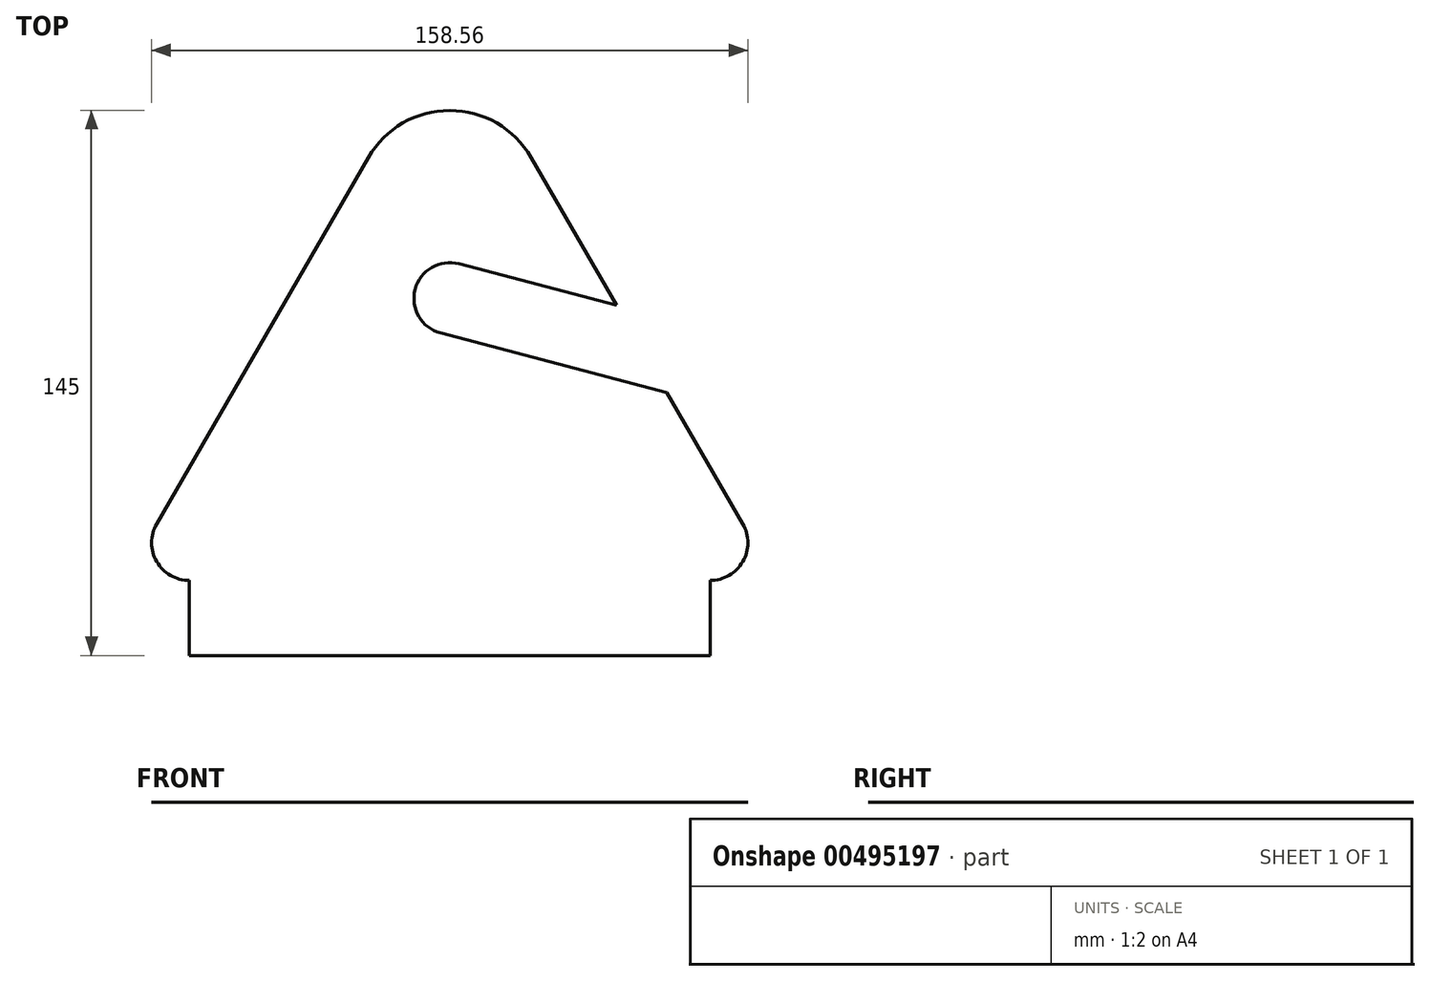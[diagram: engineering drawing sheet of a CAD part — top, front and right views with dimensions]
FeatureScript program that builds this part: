
annotation { "Feature Type Name" : "Feature", "Feature Type Description" : "" }
export const myFeature = defineFeature(function(context is Context, id is Id, definition is map)
    precondition{}
    {
        {
            var Q0;
            Q0=qCreatedBy(makeId("Top.planeOp"),FACE);
            var sketch = newSketch(context, id + "F0", { "sketchPlane" : qUnion([Q0])});
            skCircle(sketch, "E0", {"center": v(0, 0) * mm, "radius": 50 * mm, "construction": true});
            skLineSegment(sketch, "E1", {"start": v(0, 0) * mm, "end": v(0, 100) * mm, "construction": true});
            skLineSegment(sketch, "E2", {"start": v(0, 0) * mm, "end": v(-86.6, -50) * mm, "construction": true});
            skLineSegment(sketch, "E3", {"start": v(-86.6, -50) * mm, "end": v(0, 100) * mm, "construction": true});
            skCircle(sketch, "E4", {"center": v(0, 50) * mm, "radius": 25 * mm, "construction": true});
            skPoint(sketch, "E5", {"position": v(-69.28, -40) * mm});
            skCircle(sketch, "E6", {"center": v(-69.28, -40) * mm, "radius": 10 * mm, "construction": true});
            skCircle(sketch, "E7.MirrorC", {"center": v(69.28, -40) * mm, "radius": 10 * mm, "construction": true});
            skLineSegment(sketch, "E8.MirrorCS", {"start": v(0, 0) * mm, "end": v(86.6, -50) * mm, "construction": true});
            skLineSegment(sketch, "E9", {"start": v(0, 100) * mm, "end": v(86.6, -50) * mm, "construction": true});
            skLineSegment(sketch, "E10", {"start": v(86.6, -50) * mm, "end": v(-86.6, -50) * mm, "construction": true});
            skArc(sketch, "E11", {"start": v(21.65, 62.5) * mm, "mid": v(0, 75) * mm, "end": v(-21.65, 62.5) * mm});
            skArc(sketch, "E12", {"start": v(-77.94, -35) * mm, "mid": v(-77.94, -45) * mm, "end": v(-69.28, -50) * mm});
            skArc(sketch, "E13", {"start": v(69.28, -50) * mm, "mid": v(77.94, -45) * mm, "end": v(77.94, -35) * mm});
            skLineSegment(sketch, "E14", {"start": v(-21.65, 62.5) * mm, "end": v(-77.94, -35) * mm});
            skLineSegment(sketch, "E15", {"start": v(21.65, 62.5) * mm, "end": v(77.94, -35) * mm});
            skLineSegment(sketch, "E16", {"start": v(-69.28, -50) * mm, "end": v(69.28, -50) * mm});
            skLineSegment(sketch, "E17", {"start": v(-69.28, -40) * mm, "end": v(-69.28, -70) * mm, "construction": true});
            skLineSegment(sketch, "E18.bottom", {"start": v(-69.28, -70) * mm, "end": v(69.28, -70) * mm});
            skLineSegment(sketch, "E18.left", {"start": v(-69.28, -70) * mm, "end": v(-69.28, -50) * mm});
            skLineSegment(sketch, "E18.right", {"start": v(69.28, -70) * mm, "end": v(69.28, -50) * mm});
            skLineSegment(sketch, "E19", {"start": v(-69.28, -70) * mm, "end": v(-98.15, -70) * mm, "construction": true});
            skLineSegment(sketch, "E20", {"start": v(-86.6, -50) * mm, "end": v(-98.15, -70) * mm, "construction": true});
            skLineSegment(sketch, "E21.MirrorCS", {"start": v(86.6, -50) * mm, "end": v(98.15, -70) * mm, "construction": true});
            skLineSegment(sketch, "E22.MirrorCS", {"start": v(69.28, -70) * mm, "end": v(98.15, -70) * mm, "construction": true});
            skSolve(sketch);
        }
        {
            var Q0;
            Q0=makeQuery(id+"F0.imprint","IMPRINT",FACE,{"disambiguationData":[TD([[makeQuery(id+"F0.imprint","IMPRINT",EDGE,{"derivedFrom":sQuery(id+"F0.wireOp",EDGE,"E11")}),1.0]])]});
            var Q1;
            Q1=makeQuery(id+"F0.imprint","IMPRINT",FACE,{"disambiguationData":[TD([[makeQuery(id+"F0.imprint","IMPRINT",EDGE,{"derivedFrom":sQuery(id+"F0.wireOp",EDGE,"E16")}),-1.0]])]});
            extrude(context, id + "F1", {"entities" : qUnion([Q0, Q1]), "depth" : 1 / 203.2 * mm, "offsetDistance" : 25 * mm});
        }
        {
            var Q0;
            Q0=makeQuery(id+"F1.opExtrude","CAP_FACE",FACE,{"disambiguationData":[OSD([sQuery(id+"F0.wireOp",EDGE,"E11"),sQuery(id+"F0.wireOp",EDGE,"E12"),sQuery(id+"F0.wireOp",EDGE,"E13"),sQuery(id+"F0.wireOp",EDGE,"E14"),sQuery(id+"F0.wireOp",EDGE,"E15"),sQuery(id+"F0.wireOp",EDGE,"E18.bottom"),sQuery(id+"F0.wireOp",EDGE,"E18.left"),sQuery(id+"F0.wireOp",EDGE,"E18.right")])],"isStart":false});
            var sketch = newSketch(context, id + "F2", { "sketchPlane" : qUnion([Q0])});
            skCircle(sketch, "E23", {"center": v(0, 25) * mm, "radius": 9.53 * mm});
            skLineSegment(sketch, "E24", {"start": v(57.74, 0) * mm, "end": v(-2.42, 15.79) * mm});
            skLineSegment(sketch, "E25", {"start": v(44.33, 23.21) * mm, "end": v(2.42, 34.21) * mm});
            skLineSegment(sketch, "E26.0", {"start": v(21.65, 62.5) * mm, "end": v(77.94, -35) * mm});
            skLineSegment(sketch, "E27", {"start": v(0, 25) * mm, "end": v(0, 0) * mm, "construction": true});
            skSolve(sketch);
        }
        {
            var Q0;
            {var subQ0=sQuery(id+"F2.wireOp",EDGE,"E25");Q0=makeQuery(id+"F2.imprint","IMPRINT",FACE,{"disambiguationData":[TD([[makeQuery(id+"F2.imprint","IMPRINT",EDGE,{"derivedFrom":subQ0}),1.0]])]});}
            var Q1;
            {var subQ0=sQuery(id+"F2.wireOp",EDGE,"E24");var subQ1=sQuery(id+"F2.wireOp",EDGE,"E23");var subQ2=makeQuery(id+"F2.imprint","INTERSECT",VERTEX,{"disambiguationData":[OD(0.0)],"derivedFrom":[subQ1,subQ0]});Q1=makeQuery(id+"F2.imprint","IMPRINT",FACE,{"disambiguationData":[TD([[makeQuery(id+"F2.imprint","IMPRINT",EDGE,{"disambiguationData":[TD([[subQ2,1.0]])],"derivedFrom":subQ1}),1.0]])]});}
            var Q2;
            Q2=makeQuery(id+"F1.opExtrude","CAP_FACE",FACE,{"disambiguationData":[OSD([sQuery(id+"F0.wireOp",EDGE,"E11"),sQuery(id+"F0.wireOp",EDGE,"E12"),sQuery(id+"F0.wireOp",EDGE,"E13"),sQuery(id+"F0.wireOp",EDGE,"E14"),sQuery(id+"F0.wireOp",EDGE,"E15"),sQuery(id+"F0.wireOp",EDGE,"E18.bottom"),sQuery(id+"F0.wireOp",EDGE,"E18.left"),sQuery(id+"F0.wireOp",EDGE,"E18.right")])],"isStart":true});
            var Q3;
            Q3=makeQuery(id+"F1.opExtrude","SWEPT_BODY",BODY,{"disambiguationData":[OSD([sQuery(id+"F0.wireOp",EDGE,"E11"),sQuery(id+"F0.wireOp",EDGE,"E12"),sQuery(id+"F0.wireOp",EDGE,"E13"),sQuery(id+"F0.wireOp",EDGE,"E14"),sQuery(id+"F0.wireOp",EDGE,"E15"),sQuery(id+"F0.wireOp",EDGE,"E18.bottom"),sQuery(id+"F0.wireOp",EDGE,"E18.left"),sQuery(id+"F0.wireOp",EDGE,"E18.right")])]});
            extrude(context, id + "F3", {"entities" : qUnion([Q0, Q1]), "operationType" : NewBodyOperationType.REMOVE, "endBound" : BoundingType.UP_TO_SURFACE, "oppositeDirection" : true, "depth" : 25 * mm, "endBoundEntityFace" : qUnion([Q2]), "endBoundEntityBody" : qUnion([Q3]), "offsetDistance" : 25 * mm});
        }
    });
